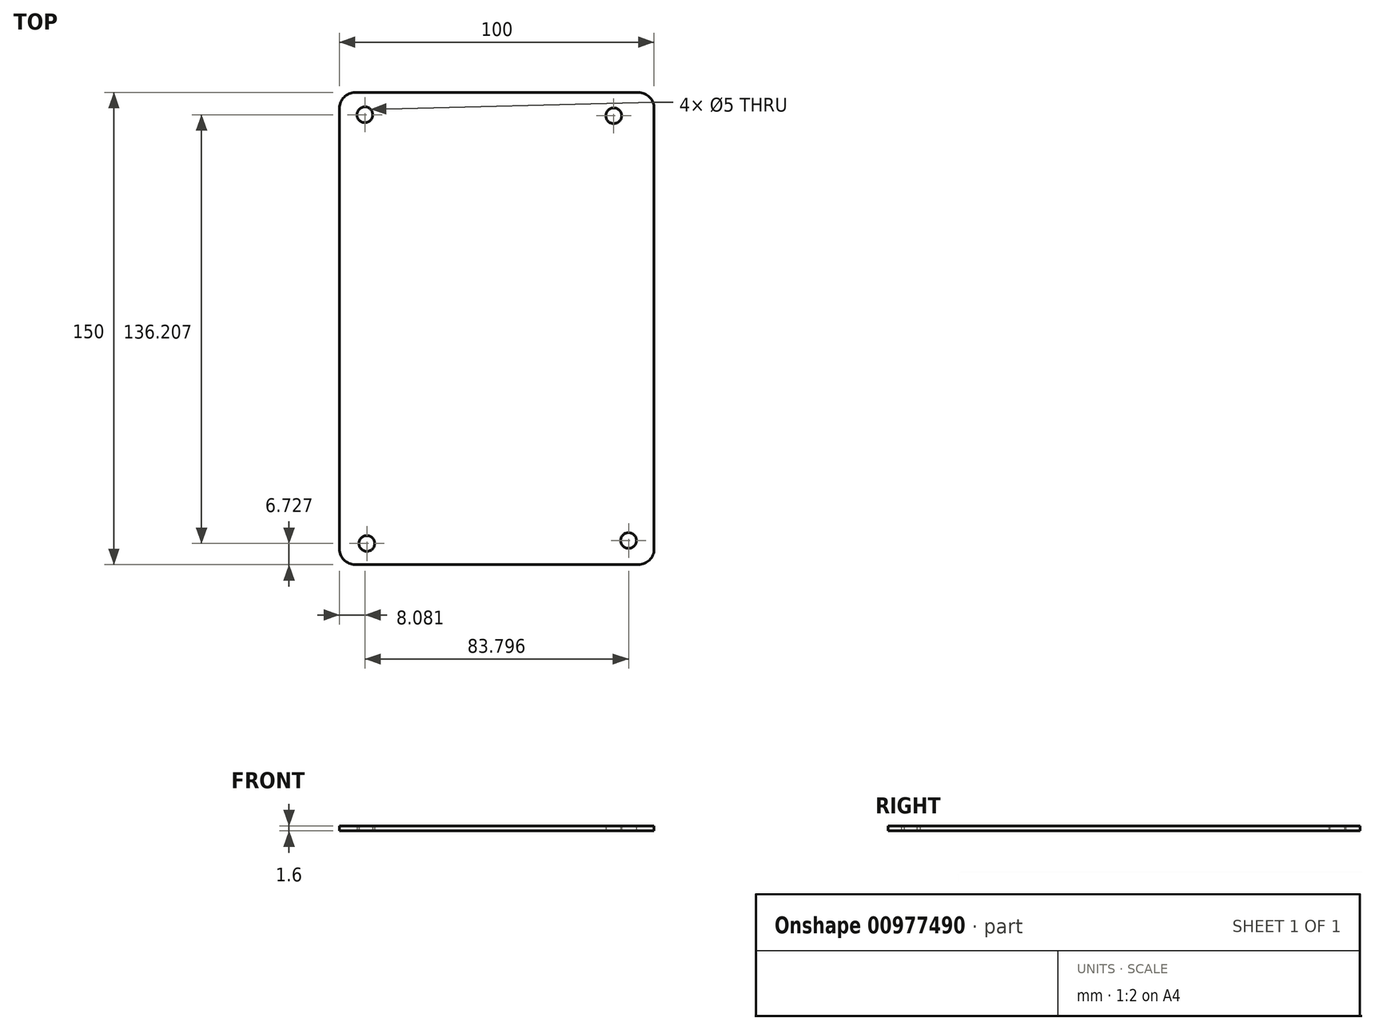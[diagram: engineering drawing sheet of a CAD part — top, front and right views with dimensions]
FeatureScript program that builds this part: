
annotation { "Feature Type Name" : "Feature", "Feature Type Description" : "" }
export const myFeature = defineFeature(function(context is Context, id is Id, definition is map)
    precondition{}
    {
        {
            var Q0;
            Q0=qCreatedBy(makeId("Top.planeOp"),FACE);
            var sketch = newSketch(context, id + "F0", { "sketchPlane" : qUnion([Q0])});
            skLineSegment(sketch, "E0.bottom", {"start": v(-50, 75) * mm, "end": v(50, 75) * mm});
            skLineSegment(sketch, "E0.top", {"start": v(-50, -75) * mm, "end": v(50, -75) * mm});
            skLineSegment(sketch, "E0.left", {"start": v(-50, 75) * mm, "end": v(-50, -75) * mm});
            skLineSegment(sketch, "E0.right", {"start": v(50, 75) * mm, "end": v(50, -75) * mm});
            skPoint(sketch, "E0.middle", {"position": v(0, 0) * mm});
            skCircle(sketch, "E1", {"center": v(-41.92, 67.93) * mm, "radius": 2.5 * mm});
            skCircle(sketch, "E2", {"center": v(37.17, 67.62) * mm, "radius": 2.5 * mm});
            skCircle(sketch, "E3", {"center": v(41.88, -67.33) * mm, "radius": 2.5 * mm});
            skCircle(sketch, "E4", {"center": v(-41.3, -68.27) * mm, "radius": 2.5 * mm});
            skSolve(sketch);
        }
        {
            var Q0;
            Q0=makeQuery(id+"F0.imprint","IMPRINT",FACE,{"disambiguationData":[TD([[makeQuery(id+"F0.imprint","IMPRINT",EDGE,{"derivedFrom":sQuery(id+"F0.wireOp",EDGE,"E0.bottom")}),-1.0]])]});
            extrude(context, id + "F1", {"entities" : qUnion([Q0]), "depth" : 1.6 * mm, "offsetDistance" : 25 * mm});
        }
        {
            var Q0;
            Q0=makeQuery(id+"F1.opExtrude","SWEPT_EDGE",EDGE,{"disambiguationData":[OSD([sQuery(id+"F0.wireOp",EDGE,"E0.bottom"),sQuery(id+"F0.wireOp",EDGE,"E0.left")])]});
            var Q1;
            Q1=makeQuery(id+"F1.opExtrude","SWEPT_EDGE",EDGE,{"disambiguationData":[OSD([sQuery(id+"F0.wireOp",EDGE,"E0.top"),sQuery(id+"F0.wireOp",EDGE,"E0.left")])]});
            var Q2;
            Q2=makeQuery(id+"F1.opExtrude","SWEPT_EDGE",EDGE,{"disambiguationData":[OSD([sQuery(id+"F0.wireOp",EDGE,"E0.top"),sQuery(id+"F0.wireOp",EDGE,"E0.right")])]});
            var Q3;
            Q3=makeQuery(id+"F1.opExtrude","SWEPT_EDGE",EDGE,{"disambiguationData":[OSD([sQuery(id+"F0.wireOp",EDGE,"E0.bottom"),sQuery(id+"F0.wireOp",EDGE,"E0.right")])]});
            fillet(context, id + "F2", {"entities" : qUnion([Q0, Q1, Q2, Q3]), "radius" : 5 * mm, "tangentPropagation" : true, "allowEdgeOverflow" : false});
        }
    });
